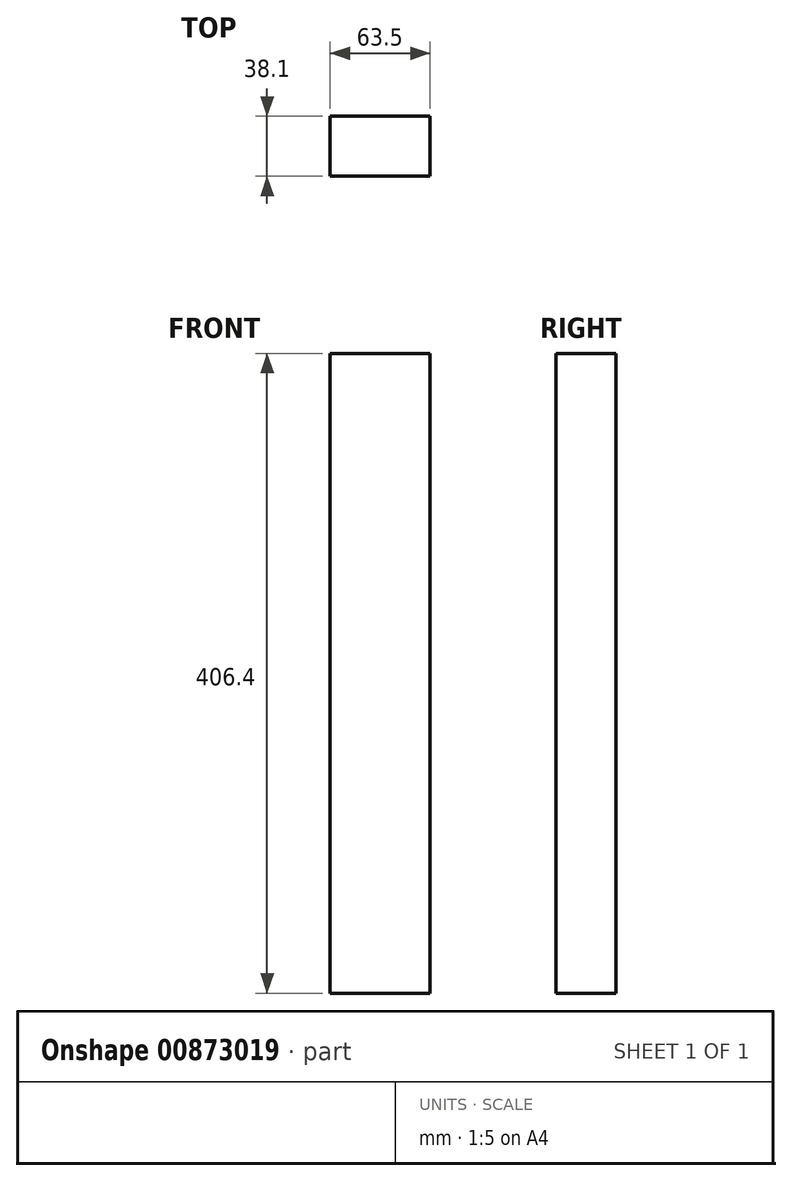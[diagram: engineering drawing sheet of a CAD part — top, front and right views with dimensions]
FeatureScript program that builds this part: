
annotation { "Feature Type Name" : "Feature", "Feature Type Description" : "" }
export const myFeature = defineFeature(function(context is Context, id is Id, definition is map)
    precondition{}
    {
        {
            var Q0;
            Q0=qCreatedBy(makeId("Top.planeOp"),FACE);
            var sketch = newSketch(context, id + "F0", { "sketchPlane" : qUnion([Q0])});
            skLineSegment(sketch, "E0.bottom", {"start": v(-270.05, -108.74) * mm, "end": v(-206.55, -108.74) * mm});
            skLineSegment(sketch, "E0.top", {"start": v(-270.05, -146.84) * mm, "end": v(-206.55, -146.84) * mm});
            skLineSegment(sketch, "E0.left", {"start": v(-270.05, -108.74) * mm, "end": v(-270.05, -146.84) * mm});
            skLineSegment(sketch, "E0.right", {"start": v(-206.55, -108.74) * mm, "end": v(-206.55, -146.84) * mm});
            skSolve(sketch);
        }
        {
            var Q0;
            Q0=makeQuery(id+"F0.imprint","IMPRINT",FACE,{"disambiguationData":[TD([[makeQuery(id+"F0.imprint","IMPRINT",EDGE,{"derivedFrom":sQuery(id+"F0.wireOp",EDGE,"E0.bottom")}),-1.0]])]});
            extrude(context, id + "F1", {"entities" : qUnion([Q0]), "depth" : 406.4 * mm, "offsetDistance" : 25.4 * mm});
        }
    });
